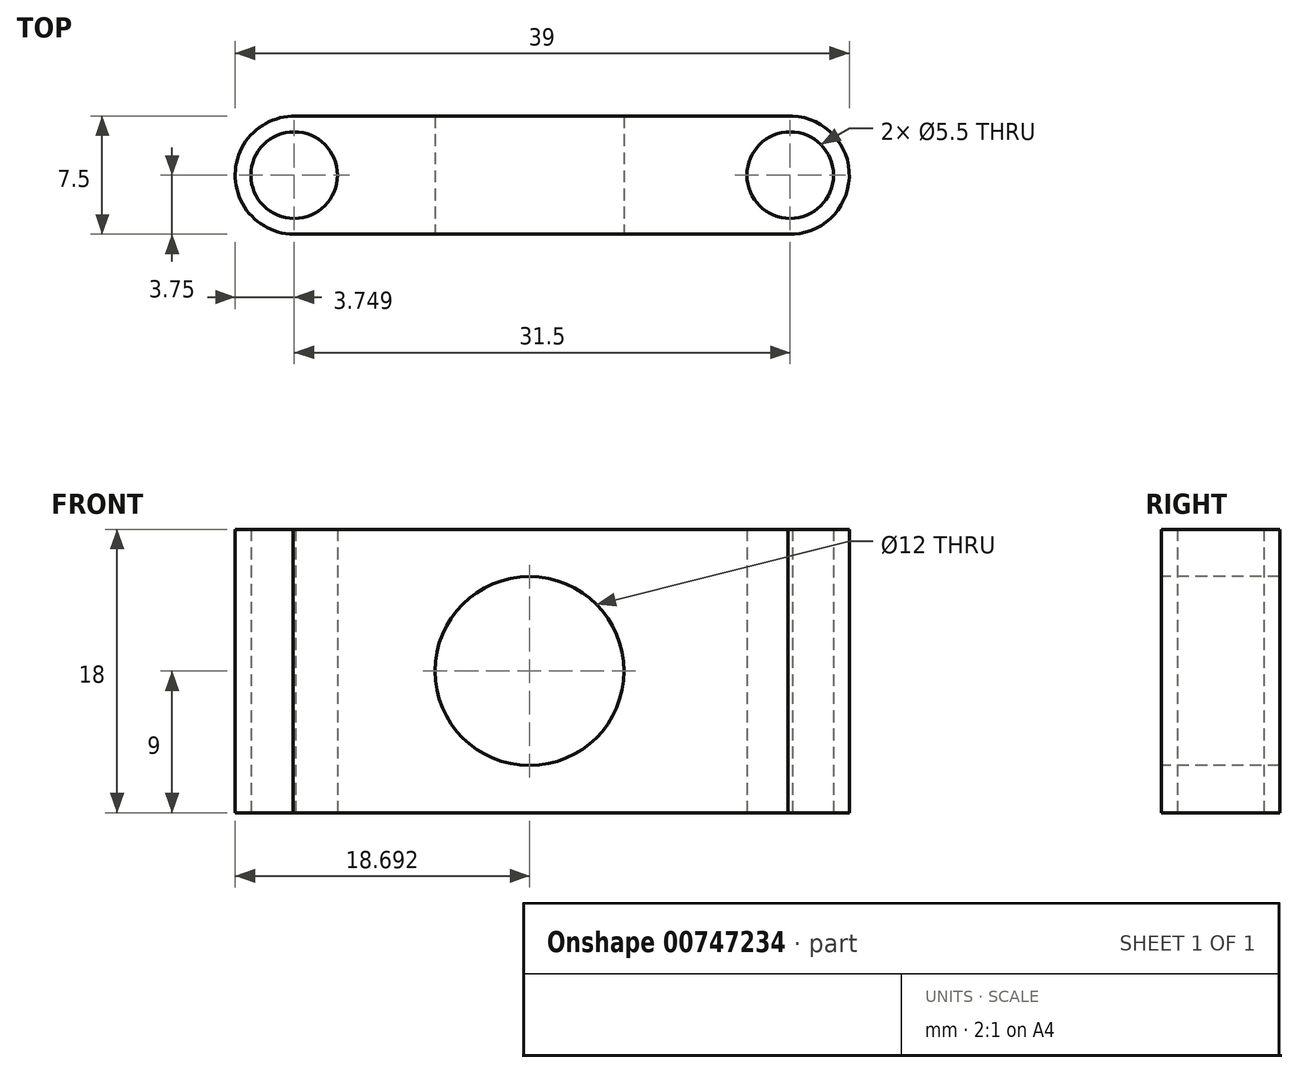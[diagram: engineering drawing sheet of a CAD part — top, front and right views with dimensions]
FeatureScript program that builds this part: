
annotation { "Feature Type Name" : "Feature", "Feature Type Description" : "" }
export const myFeature = defineFeature(function(context is Context, id is Id, definition is map)
    precondition{}
    {
        {
            var Q0;
            Q0=qCreatedBy(makeId("Top.planeOp"),FACE);
            var sketch = newSketch(context, id + "F0", { "sketchPlane" : qUnion([Q0])});
            skLineSegment(sketch, "E0.top", {"start": v(16.56, 0) * mm, "end": v(-14.94, 0) * mm, "construction": true});
            skPoint(sketch, "E0.middle", {"position": v(0, 0) * mm});
            skCircle(sketch, "E1", {"center": v(-14.94, 0) * mm, "radius": 2.75 * mm});
            skCircle(sketch, "E2", {"center": v(16.56, 0) * mm, "radius": 2.75 * mm});
            skCircle(sketch, "E3", {"center": v(-14.94, 0) * mm, "radius": 3.75 * mm});
            skCircle(sketch, "E4", {"center": v(16.56, 0) * mm, "radius": 3.75 * mm});
            skLineSegment(sketch, "E5", {"start": v(-15, -3.75) * mm, "end": v(16.42, -3.75) * mm});
            skLineSegment(sketch, "E6", {"start": v(16.7, 3.75) * mm, "end": v(-14.86, 3.75) * mm});
            skLineSegment(sketch, "E7", {"start": v(-11.2, 0) * mm, "end": v(12.8, 0) * mm});
            skSolve(sketch);
        }
        {
            var Q0;
            {var subQ3=sQuery(id+"F0.wireOp",EDGE,"E7");Q0=makeQuery(id+"F0.imprint","IMPRINT",FACE,{"disambiguationData":[TD([[makeQuery(id+"F0.imprint","IMPRINT",EDGE,{"derivedFrom":subQ3}),1.0]])]});}
            var Q1;
            Q1=makeQuery(id+"F0.imprint","IMPRINT",FACE,{"disambiguationData":[TD([[makeQuery(id+"F0.imprint","IMPRINT",EDGE,{"derivedFrom":sQuery(id+"F0.wireOp",EDGE,"E1")}),-1.0]])]});
            var Q2;
            Q2=makeQuery(id+"F0.imprint","IMPRINT",FACE,{"disambiguationData":[TD([[makeQuery(id+"F0.imprint","IMPRINT",EDGE,{"derivedFrom":sQuery(id+"F0.wireOp",EDGE,"E2")}),-1.0]])]});
            var Q3;
            {var subQ0=sQuery(id+"F0.wireOp",EDGE,"E7");Q3=makeQuery(id+"F0.imprint","IMPRINT",FACE,{"disambiguationData":[TD([[makeQuery(id+"F0.imprint","IMPRINT",EDGE,{"derivedFrom":subQ0}),-1.0]])]});}
            extrude(context, id + "F1", {"entities" : qUnion([Q0, Q1, Q2, Q3]), "depth" : 18 * mm, "offsetDistance" : 25 * mm});
        }
        {
            var Q0;
            Q0=makeQuery(id+"F1.opExtrude","SWEPT_FACE",FACE,{"disambiguationData":[OSD([sQuery(id+"F0.wireOp",EDGE,"E5")])]});
            var sketch = newSketch(context, id + "F2", { "sketchPlane" : qUnion([Q0])});
            skCircle(sketch, "E8", {"center": v(0, 9) * mm, "radius": 6 * mm});
            skSolve(sketch);
        }
        {
            var Q0;
            Q0=makeQuery(id+"F2.imprint","IMPRINT",FACE,{"disambiguationData":[TD([[makeQuery(id+"F2.imprint","IMPRINT",EDGE,{"derivedFrom":sQuery(id+"F2.wireOp",EDGE,"368db3a1-3959-45b8-8e8b-fa4350194cae")}),1.0]])]});
            var Q1;
            Q1=makeQuery(id+"F2.imprint","IMPRINT",FACE,{"disambiguationData":[TD([[makeQuery(id+"F2.imprint","IMPRINT",EDGE,{"derivedFrom":sQuery(id+"F2.wireOp",EDGE,"E8")}),1.0]])]});
            extrude(context, id + "F3", {"entities" : qUnion([Q0, Q1]), "operationType" : NewBodyOperationType.REMOVE, "endBound" : BoundingType.THROUGH_ALL, "oppositeDirection" : true, "depth" : 25 * mm, "offsetDistance" : 25 * mm});
        }
    });
